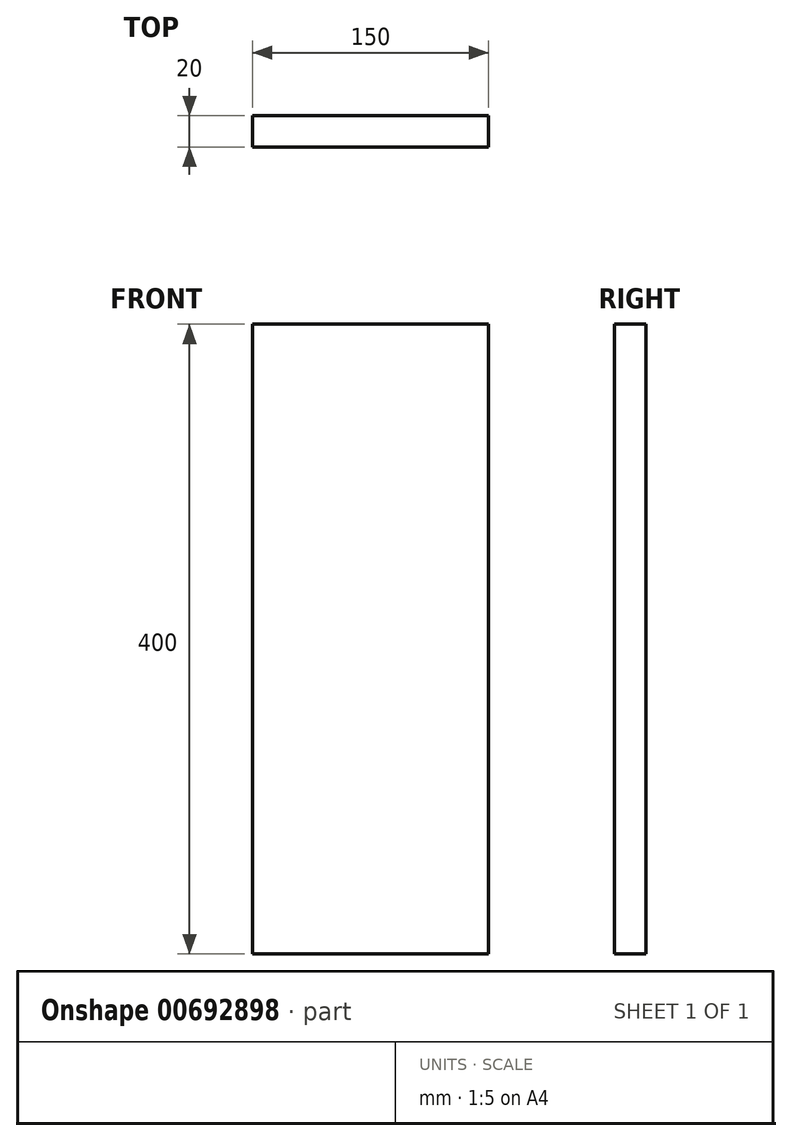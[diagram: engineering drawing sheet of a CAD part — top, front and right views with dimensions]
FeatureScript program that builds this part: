
annotation { "Feature Type Name" : "Feature", "Feature Type Description" : "" }
export const myFeature = defineFeature(function(context is Context, id is Id, definition is map)
    precondition{}
    {
        {
            var Q0;
            Q0=qCreatedBy(makeId("Front.planeOp"),FACE);
            var sketch = newSketch(context, id + "F0", { "sketchPlane" : qUnion([Q0])});
            skLineSegment(sketch, "E0.bottom", {"start": v(-150, 400) * mm, "end": v(0, 400) * mm});
            skLineSegment(sketch, "E0.top", {"start": v(-150, 0) * mm, "end": v(0, 0) * mm});
            skLineSegment(sketch, "E0.left", {"start": v(-150, 400) * mm, "end": v(-150, 0) * mm});
            skLineSegment(sketch, "E0.right", {"start": v(0, 400) * mm, "end": v(0, 0) * mm});
            skSolve(sketch);
        }
        {
            var Q0;
            Q0=makeQuery(id+"F0.imprint","IMPRINT",FACE,{"disambiguationData":[TD([[makeQuery(id+"F0.imprint","IMPRINT",EDGE,{"derivedFrom":sQuery(id+"F0.wireOp",EDGE,"E0.bottom")}),-1.0]])]});
            extrude(context, id + "F1", {"entities" : qUnion([Q0]), "depth" : 20 * mm, "offsetDistance" : 25 * mm});
        }
    });
